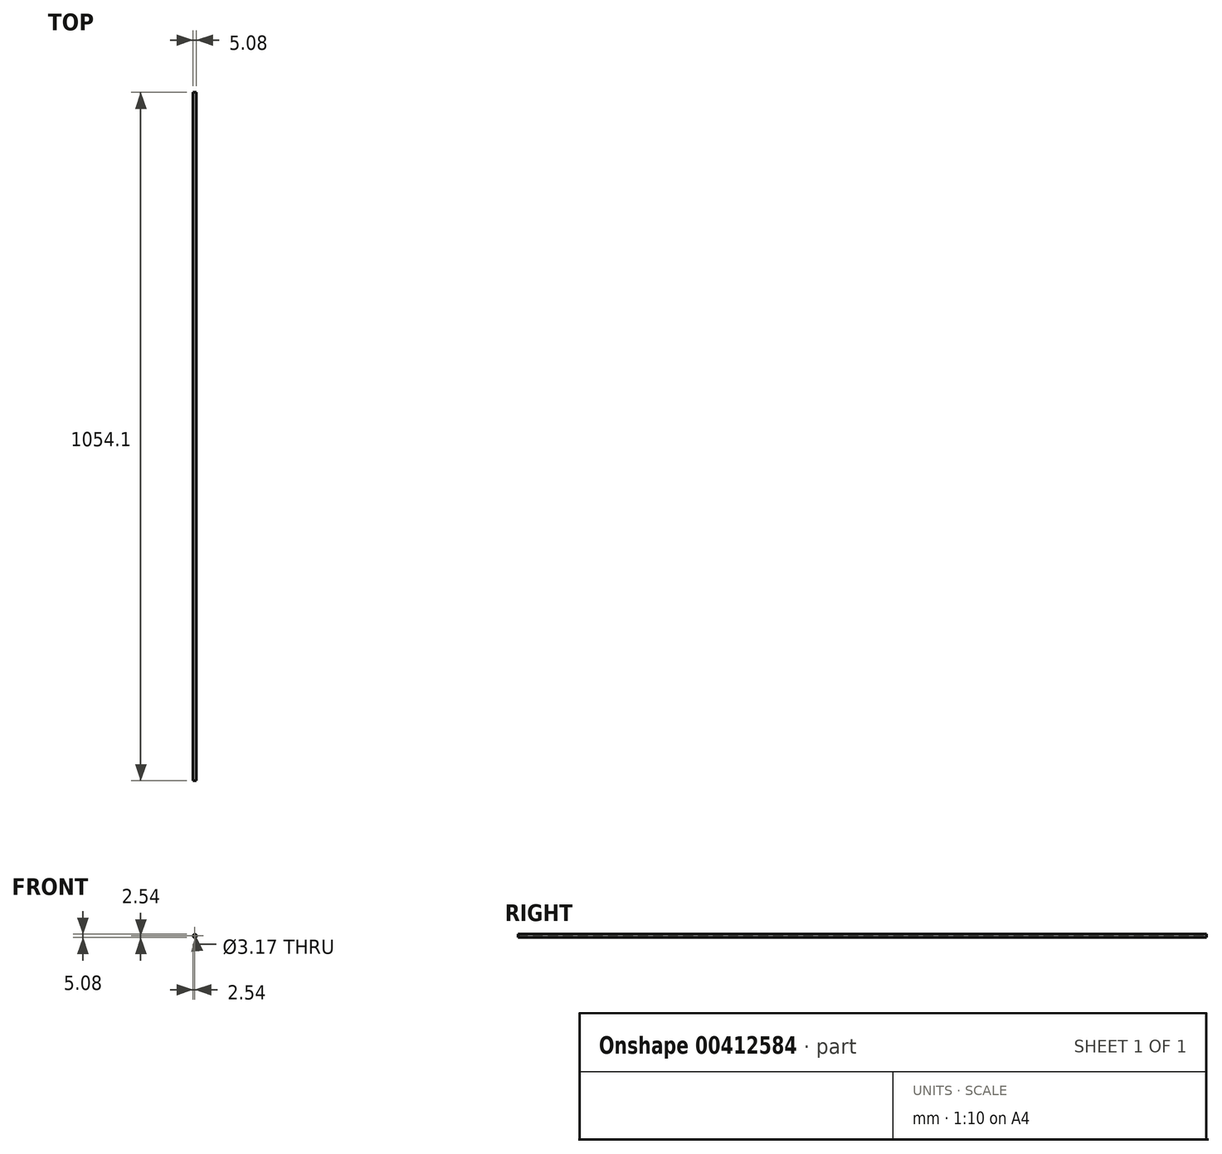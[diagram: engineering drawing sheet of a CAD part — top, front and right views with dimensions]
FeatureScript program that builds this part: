
annotation { "Feature Type Name" : "Feature", "Feature Type Description" : "" }
export const myFeature = defineFeature(function(context is Context, id is Id, definition is map)
    precondition{}
    {
        {
            var Q0;
            Q0=qCreatedBy(makeId("Front.planeOp"),FACE);
            var sketch = newSketch(context, id + "F0", { "sketchPlane" : qUnion([Q0])});
            skCircle(sketch, "E0", {"center": v(0, 0) * mm, "radius": 2.54 * mm});
            skCircle(sketch, "E1", {"center": v(0, 0) * mm, "radius": 1.59 * mm});
            skSolve(sketch);
        }
        {
            var Q0;
            Q0=makeQuery(id+"F0.imprint","IMPRINT",FACE,{"disambiguationData":[TD([[makeQuery(id+"F0.imprint","IMPRINT",EDGE,{"derivedFrom":sQuery(id+"F0.wireOp",EDGE,"E0")}),1.0]])]});
            extrude(context, id + "F1", {"entities" : qUnion([Q0]), "depth" : 1054.1 * mm});
        }
    });
